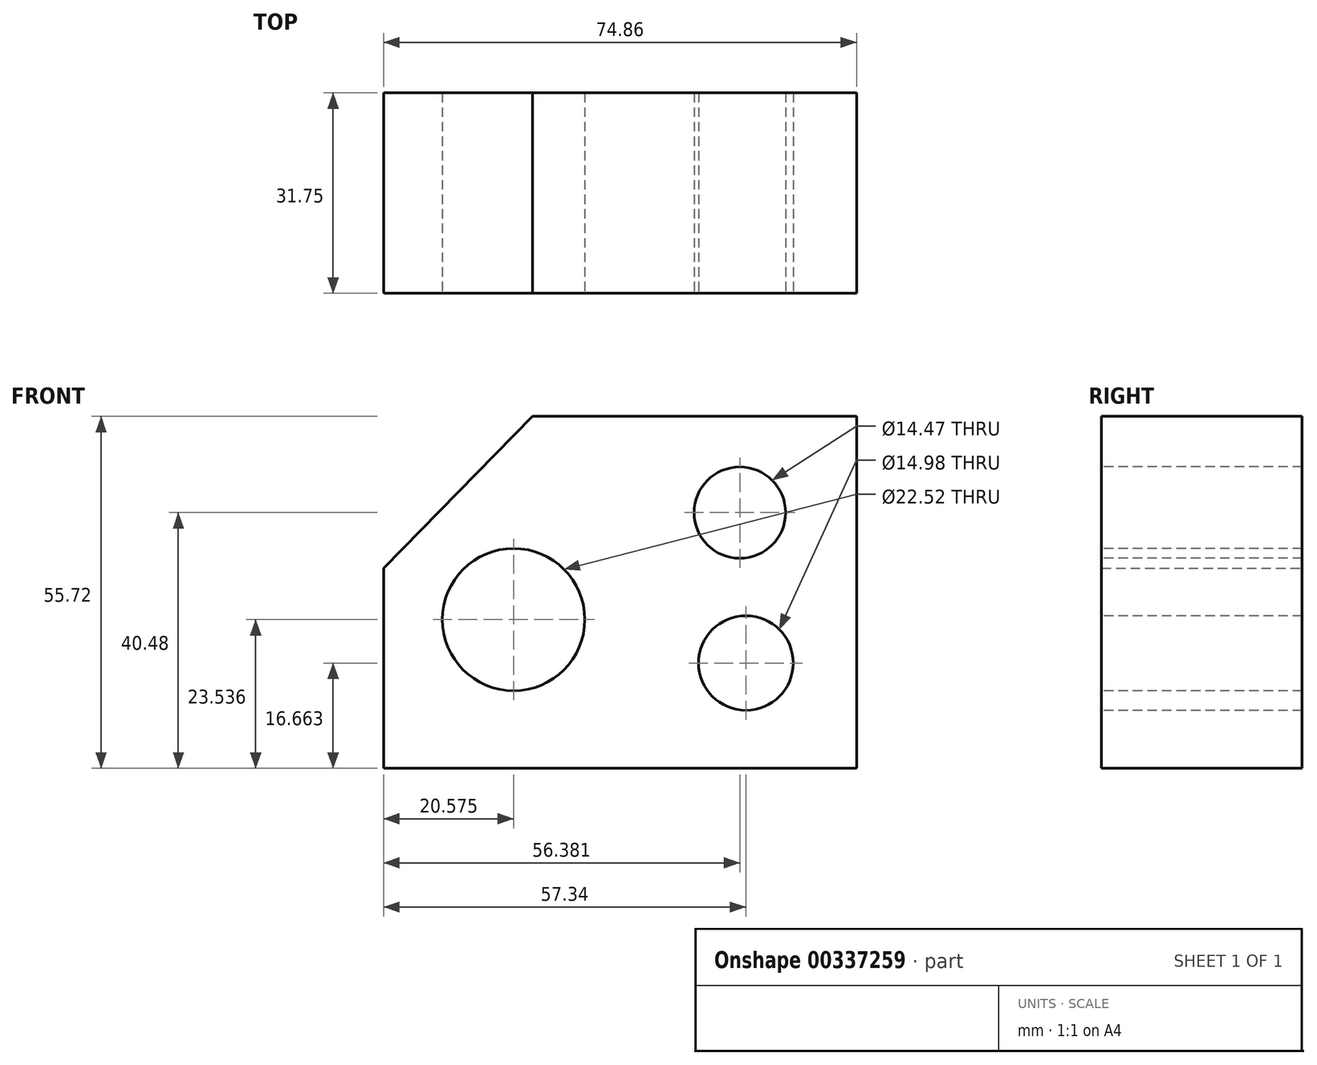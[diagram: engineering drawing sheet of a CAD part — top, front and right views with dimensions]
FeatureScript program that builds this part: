
annotation { "Feature Type Name" : "Feature", "Feature Type Description" : "" }
export const myFeature = defineFeature(function(context is Context, id is Id, definition is map)
    precondition{}
    {
        {
            var Q0;
            Q0=qCreatedBy(makeId("Front.planeOp"),FACE);
            var sketch = newSketch(context, id + "F0", { "sketchPlane" : qUnion([Q0])});
            skLineSegment(sketch, "E0", {"start": v(0, 36.81) * mm, "end": v(23.56, 60.87) * mm});
            skLineSegment(sketch, "E1", {"start": v(23.56, 60.87) * mm, "end": v(74.86, 60.87) * mm});
            skLineSegment(sketch, "E2", {"start": v(74.86, 60.87) * mm, "end": v(74.86, 5.15) * mm});
            skLineSegment(sketch, "E3", {"start": v(74.86, 5.15) * mm, "end": v(0, 5.15) * mm});
            skLineSegment(sketch, "E4", {"start": v(0, 5.15) * mm, "end": v(0, 36.81) * mm});
            skSolve(sketch);
        }
        {
            var Q0;
            Q0=makeQuery(id+"F0.imprint","IMPRINT",FACE,{"disambiguationData":[TD([[makeQuery(id+"F0.imprint","IMPRINT",EDGE,{"derivedFrom":sQuery(id+"F0.wireOp",EDGE,"E0")}),-1.0]])]});
            extrude(context, id + "F1", {"entities" : qUnion([Q0]), "depth" : 31.75 * mm});
        }
        {
            var Q0;
            Q0=makeQuery(id+"F1.opExtrude","CAP_FACE",FACE,{"disambiguationData":[OSD([sQuery(id+"F0.wireOp",EDGE,"E0"),sQuery(id+"F0.wireOp",EDGE,"E1"),sQuery(id+"F0.wireOp",EDGE,"E2"),sQuery(id+"F0.wireOp",EDGE,"E3"),sQuery(id+"F0.wireOp",EDGE,"E4")])],"isStart":false});
            var sketch = newSketch(context, id + "F2", { "sketchPlane" : qUnion([Q0])});
            skCircle(sketch, "E5", {"center": v(56.38, 45.63) * mm, "radius": 7.24 * mm});
            skCircle(sketch, "E6", {"center": v(57.34, 21.81) * mm, "radius": 7.5 * mm});
            skCircle(sketch, "E7", {"center": v(20.58, 28.69) * mm, "radius": 11.26 * mm});
            skSolve(sketch);
        }
        {
            var Q0;
            Q0=makeQuery(id+"F2.imprint","IMPRINT",FACE,{"disambiguationData":[TD([[makeQuery(id+"F2.imprint","IMPRINT",EDGE,{"derivedFrom":sQuery(id+"F2.wireOp",EDGE,"E5")}),1.0]])]});
            var Q1;
            Q1=makeQuery(id+"F2.imprint","IMPRINT",FACE,{"disambiguationData":[TD([[makeQuery(id+"F2.imprint","IMPRINT",EDGE,{"derivedFrom":sQuery(id+"F2.wireOp",EDGE,"E6")}),1.0]])]});
            var Q2;
            Q2=makeQuery(id+"F2.imprint","IMPRINT",FACE,{"disambiguationData":[TD([[makeQuery(id+"F2.imprint","IMPRINT",EDGE,{"derivedFrom":sQuery(id+"F2.wireOp",EDGE,"E7")}),1.0]])]});
            extrude(context, id + "F3", {"entities" : qUnion([Q0, Q1, Q2]), "operationType" : NewBodyOperationType.REMOVE, "depth" : -76.2 * mm});
        }
    });
